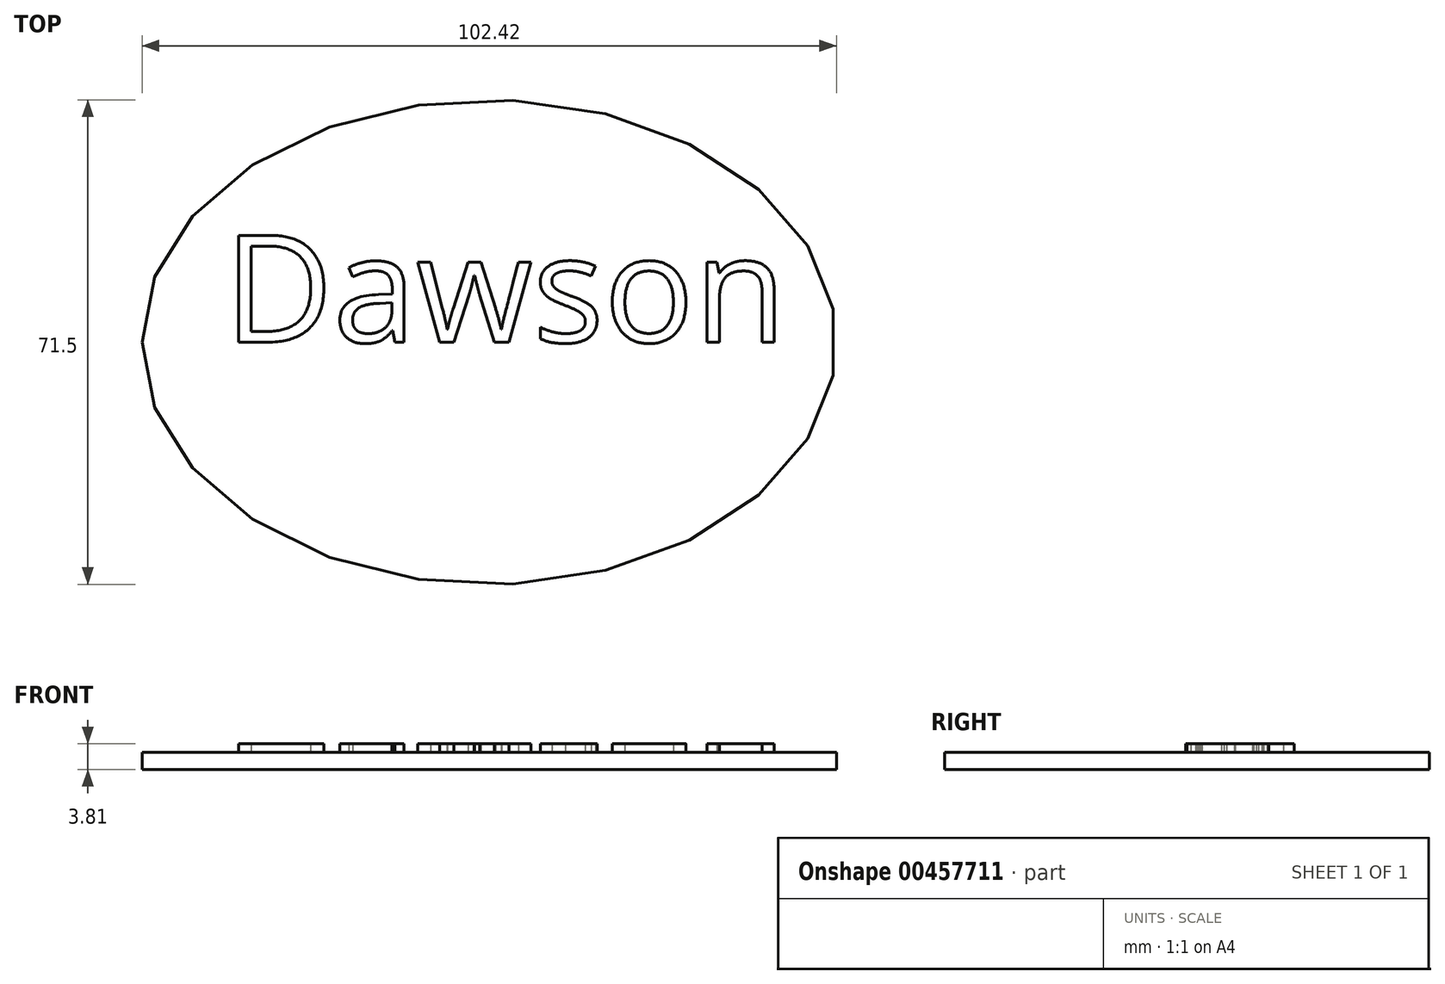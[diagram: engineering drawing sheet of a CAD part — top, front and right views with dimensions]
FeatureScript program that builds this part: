
annotation { "Feature Type Name" : "Feature", "Feature Type Description" : "" }
export const myFeature = defineFeature(function(context is Context, id is Id, definition is map)
    precondition{}
    {
        {
            var Q0;
            Q0=qCreatedBy(makeId("Top.planeOp"),FACE);
            var sketch = newSketch(context, id + "F0", { "sketchPlane" : qUnion([Q0])});
            skEllipse(sketch, "E0", {"center": v(0, 0) * mm, "majorRadius": 51.21 * mm, "minorRadius": 35.75 * mm, "majorAxis": v(-1, 0)});
            skSolve(sketch);
        }
        {
            var Q0;
            Q0 = qSketchRegion(id + "F0", true);
            extrude(context, id + "F1", {"entities" : qUnion([Q0]), "depth" : 2.54 * mm});
        }
        {
            var Q0;
            Q0=qCreatedBy(makeId("Top.planeOp"),FACE);
            var sketch = newSketch(context, id + "F2", { "sketchPlane" : qUnion([Q0])});
            skText(sketch, "E1", { "text": "Dawson ", "fontName": "OpenSans-Regular.ttf"});
            const initialGuessF2  = {"E1": [-0.03913, 0, 1, 0, 0.01589]};
            skSetInitialGuess(sketch, initialGuessF2);
            skSolve(sketch);
        }
        {
            var Q0;
            Q0 = qSketchRegion(id + "F2", true);
            extrude(context, id + "F3", {"entities" : qUnion([Q0]), "operationType" : NewBodyOperationType.ADD, "depth" : 3.8 * mm});
        }
    });
